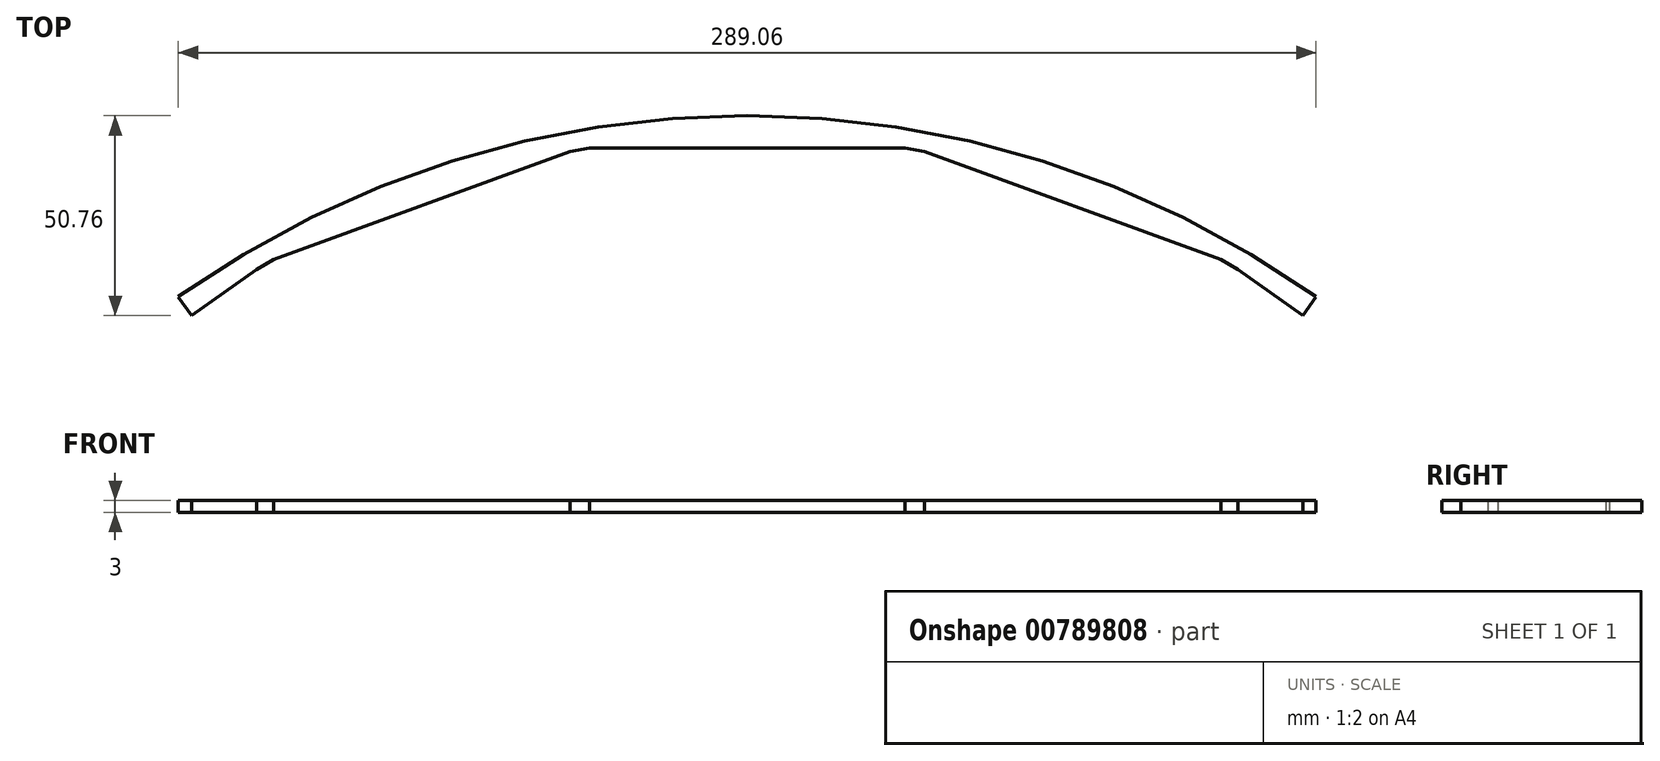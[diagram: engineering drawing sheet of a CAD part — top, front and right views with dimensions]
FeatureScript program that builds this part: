
annotation { "Feature Type Name" : "Feature", "Feature Type Description" : "" }
export const myFeature = defineFeature(function(context is Context, id is Id, definition is map)
    precondition{}
    {
        {
            var Q0;
            Q0=qCreatedBy(makeId("Top.planeOp"),FACE);
            var sketch = newSketch(context, id + "F0", { "sketchPlane" : qUnion([Q0])});
            skLineSegment(sketch, "E0", {"start": v(0, 0) * mm, "end": v(-160.7, 191.51) * mm});
            skLineSegment(sketch, "E1", {"start": v(0, 0) * mm, "end": v(160.7, 191.51) * mm});
            skArc(sketch, "E2", {"start": v(160.7, 191.51) * mm, "mid": v(0, 250) * mm, "end": v(-160.7, 191.51) * mm});
            skLineSegment(sketch, "E3", {"start": v(-124.67, 210.93) * mm, "end": v(-157.48, 187.68) * mm});
            skLineSegment(sketch, "E4", {"start": v(-120.33, 213.43) * mm, "end": v(-45, 240.84) * mm});
            skLineSegment(sketch, "E5", {"start": v(-40.08, 241.71) * mm, "end": v(40.08, 241.71) * mm});
            skLineSegment(sketch, "E6", {"start": v(45, 240.84) * mm, "end": v(120.33, 213.43) * mm});
            skLineSegment(sketch, "E7", {"start": v(124.67, 210.93) * mm, "end": v(157.48, 187.68) * mm});
            skLineSegment(sketch, "E8", {"start": v(-157.48, 187.68) * mm, "end": v(-160.7, 191.51) * mm});
            skLineSegment(sketch, "E9", {"start": v(157.48, 187.68) * mm, "end": v(160.7, 191.51) * mm});
            skLineSegment(sketch, "E10", {"start": v(-124.67, 210.93) * mm, "end": v(-120.33, 213.43) * mm});
            skLineSegment(sketch, "E11", {"start": v(-45, 240.84) * mm, "end": v(-40.08, 241.71) * mm});
            skLineSegment(sketch, "E12", {"start": v(40.08, 241.71) * mm, "end": v(45, 240.84) * mm});
            skLineSegment(sketch, "E13", {"start": v(120.33, 213.43) * mm, "end": v(124.67, 210.93) * mm});
            skLineSegment(sketch, "E14", {"start": v(-141.16, 199.24) * mm, "end": v(-144.53, 204) * mm});
            skLineSegment(sketch, "E15", {"start": v(141.16, 199.24) * mm, "end": v(144.53, 204) * mm});
            skSolve(sketch);
        }
        {
            var Q0;
            Q0=makeQuery(id+"F0.imprint","IMPRINT",FACE,{"disambiguationData":[TD([[makeQuery(id+"F0.imprint","IMPRINT",EDGE,{"derivedFrom":sQuery(id+"F0.wireOp",EDGE,"E4")}),1.0]])]});
            extrude(context, id + "F1", {"entities" : qUnion([Q0]), "depth" : 3 * mm, "offsetDistance" : 25 * mm});
        }
    });
